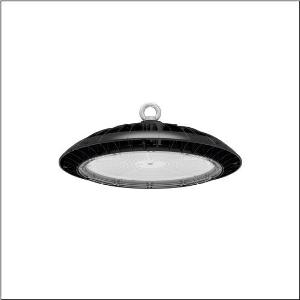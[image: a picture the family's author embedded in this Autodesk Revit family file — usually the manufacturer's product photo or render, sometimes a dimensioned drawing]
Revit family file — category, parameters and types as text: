
# Revit family: highbay_42-l_51hp32mb7mma
name_source: partatom
category: Lighting Fixtures
units: mm (PartAtom-declared; Revit-internal decimal feet)

## family parameters
Cut with Voids When Loaded = No
Host = Face
Light Source = No
Part Type = Normal
Room Calculation Point = No
Round Connector Dimension = Use Diameter
Shared = No

## types (1)
- --- (1 x LED, 28000 lm, 175 W, 5700K)
    Apparent Load = 175 VA
    CIE Flux Codes = 49 82 98 100 100
    Color Rendering = 80
    Color Temperature = 5700K
    Default Elevation = 1800 mm
    Description = Highbay 42-L, LED high bay luminaire, primary light control with lens, of PC, primary optical cover: cover panel, of PC, transparent, light emission: direct distribution, primary light characteristic: rotationally symmetric, installation type: suspended mounting, surface-mounted, LED, rated luminous flux: 28.000lm, luminous efficacy: 160lm/W, light colour: 857, colour temperature: 5700K, control gear: ECG, with cable, 3x 1.0mm², free wire ends, mains connection: 230V, AC, 50Hz, cable length: 1,5m, rated input power: 175W, housing, rotationally symmetric, of diecast aluminium, black, with hook on luminaire side, diameter: 305mm, height: 117mm, protection rating (complete): IP65, insulation class (complete): insulation class I (protective earthing), certification: CE, UKCA, protection symbol: D, impact resistance: IK08, permissible operating ambient temperature: -20..+40°C, corresponds to IFS (International Featured Standards) requirements for safety and quality in the food industry, packaging unit: 1 piece
    Height = 117 mm
    Lamp = 1 x LED
    Lamp Light Flux = 28000 lm
    Lamp Power = 175 W
    Lamp count = 1
    Length = 305 mm
    Luminous efficacy = 160 lm/W
    Manufacturer = Siteco
    ModVariant = No
    Model = 51HP32MB7MMA
    Mounting Place = Ceiling
    Mounting Type = Pendant
    Number of Poles = 1
    OnlyDefault = Yes
    Power Factor = 1
    Product Name = Highbay 42-L
    Product group = LED high bay luminaire
    ProductGroupID = 903
    Protection Class = Protection class I
    Protection Degree = IP 65
    RLX_Detail_Level = 1
    RLX_Emergency_Light_Flux = 0 lm
    RLX_Emergency_Type = 0
    RLX_Emergency_Type_DB = No
    RlxData = <blob elided: 286837 chars, md5=995595f3>
    Socket = socket
    Standby Power = 0 W
    System Light Flux = 28000 lm
    System Power = 175 W
    Type Comments = factory setting: luminous flux: 100 % | (OFF | OFF | OFF)
    Type Image = l_1003932.jpg
    URL = http://relux.com
    VarID = @adj_135323
    Voltage = 0 V
    Weight = 0.00 kg
    Width = 0 mm  [stored 0 ft]

note: [stored X ft] marks values corroborated as IEEE doubles in the binary element streams (Revit-internal decimal feet)

## geometry (parser evidence)
native form markers: Blend x4, Sweep x11
no freeform markers — native parametric forms only
